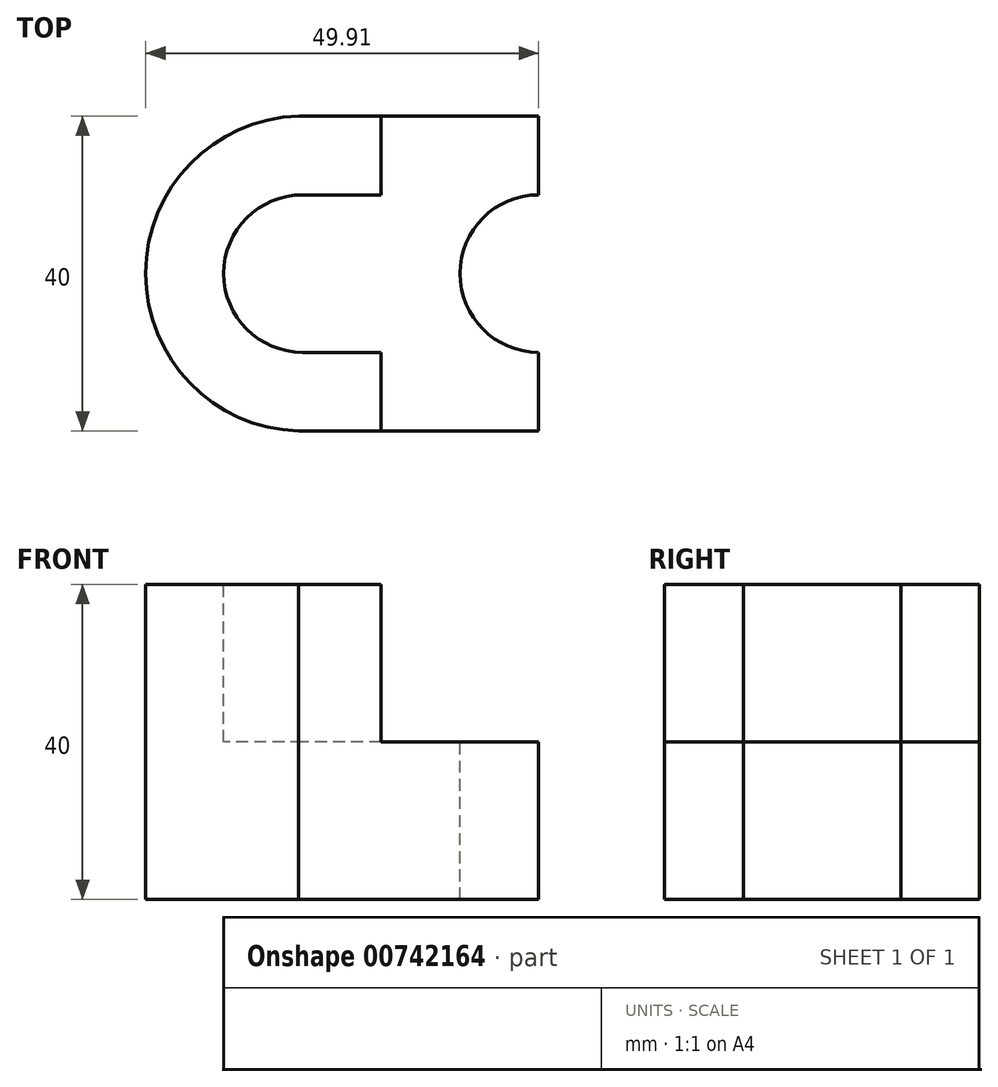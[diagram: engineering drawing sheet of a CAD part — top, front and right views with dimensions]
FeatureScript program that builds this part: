
annotation { "Feature Type Name" : "Feature", "Feature Type Description" : "" }
export const myFeature = defineFeature(function(context is Context, id is Id, definition is map)
    precondition{}
    {
        {
            var Q0;
            Q0=qCreatedBy(makeId("Front.planeOp"),FACE);
            var sketch = newSketch(context, id + "F0", { "sketchPlane" : qUnion([Q0])});
            skLineSegment(sketch, "E0", {"start": v(0, 0) * mm, "end": v(50, 0) * mm});
            skLineSegment(sketch, "E1", {"start": v(50, 0) * mm, "end": v(50, 20) * mm});
            skLineSegment(sketch, "E2", {"start": v(50, 20) * mm, "end": v(30, 20) * mm});
            skLineSegment(sketch, "E3", {"start": v(30, 20) * mm, "end": v(30, 40) * mm});
            skLineSegment(sketch, "E4", {"start": v(30, 40) * mm, "end": v(0, 40) * mm});
            skLineSegment(sketch, "E5", {"start": v(0, 40) * mm, "end": v(0, 0) * mm});
            skSolve(sketch);
        }
        {
            var Q0;
            Q0=makeQuery(id+"F0.imprint","IMPRINT",FACE,{"disambiguationData":[TD([[makeQuery(id+"F0.imprint","IMPRINT",EDGE,{"derivedFrom":sQuery(id+"F0.wireOp",EDGE,"E0")}),1.0]])]});
            extrude(context, id + "F1", {"entities" : qUnion([Q0]), "depth" : 40 * mm, "offsetDistance" : 25 * mm});
        }
        {
            var Q0;
            Q0=makeQuery(id+"F1.opExtrude","SWEPT_FACE",FACE,{"disambiguationData":[OSD([sQuery(id+"F0.wireOp",EDGE,"E4")])]});
            var sketch = newSketch(context, id + "F2", { "sketchPlane" : qUnion([Q0])});
            skArc(sketch, "E6", {"start": v(19.56, 0) * mm, "mid": v(0.1, -20.57) * mm, "end": v(20.7, -40) * mm});
            skSolve(sketch);
        }
        {
            var Q0;
            {var subQ1=sQuery(id+"F0.wireOp",EDGE,"E4");var subQ6=makeQuery(id+"F1.opExtrude","SWEPT_EDGE",EDGE,{"disambiguationData":[OSD([subQ1,sQuery(id+"F0.wireOp",EDGE,"E5")])]});Q0=makeQuery(id+"F2.imprint","IMPRINT",FACE,{"disambiguationData":[TD([[makeQuery(id+"F2.imprint","IMPRINT",EDGE,{"derivedFrom":subQ6}),-1.0]])]});}
            extrude(context, id + "F3", {"entities" : qUnion([Q0]), "operationType" : NewBodyOperationType.REMOVE, "oppositeDirection" : true, "depth" : 40 * mm, "offsetDistance" : 25 * mm});
        }
        {
            var Q0;
            Q0=makeQuery(id+"F1.opExtrude","SWEPT_FACE",FACE,{"disambiguationData":[OSD([sQuery(id+"F0.wireOp",EDGE,"E4")])]});
            var sketch = newSketch(context, id + "F4", { "sketchPlane" : qUnion([Q0])});
            skLineSegment(sketch, "E7", {"start": v(30, 0) * mm, "end": v(30, -10) * mm});
            skLineSegment(sketch, "E8", {"start": v(30, -10) * mm, "end": v(20, -10) * mm});
            skLineSegment(sketch, "E9", {"start": v(20, -10) * mm, "end": v(20, -30) * mm});
            skLineSegment(sketch, "E10", {"start": v(20, -30) * mm, "end": v(30, -30) * mm});
            skLineSegment(sketch, "E11", {"start": v(30, -30) * mm, "end": v(30, -40) * mm});
            skLineSegment(sketch, "E12", {"start": v(30, -10) * mm, "end": v(30, -30) * mm});
            skSolve(sketch);
        }
        {
            var Q0;
            Q0=makeQuery(id+"F4.imprint","IMPRINT",FACE,{"disambiguationData":[TD([[makeQuery(id+"F4.imprint","IMPRINT",EDGE,{"derivedFrom":sQuery(id+"F4.wireOp",EDGE,"E8")}),1.0]])]});
            extrude(context, id + "F5", {"entities" : qUnion([Q0]), "operationType" : NewBodyOperationType.REMOVE, "oppositeDirection" : true, "depth" : 20 * mm, "offsetDistance" : 25 * mm});
        }
        {
            var Q0;
            Q0=makeQuery(id+"F1.opExtrude","SWEPT_FACE",FACE,{"disambiguationData":[OSD([sQuery(id+"F0.wireOp",EDGE,"E4")])]});
            var sketch = newSketch(context, id + "F6", { "sketchPlane" : qUnion([Q0])});
            skArc(sketch, "E13", {"start": v(20, -10) * mm, "mid": v(10, -20) * mm, "end": v(20, -30) * mm});
            skSolve(sketch);
        }
        {
            var Q0;
            Q0=makeQuery(id+"F6.imprint","IMPRINT",FACE,{"disambiguationData":[TD([[makeQuery(id+"F6.imprint","IMPRINT",EDGE,{"derivedFrom":sQuery(id+"F6.wireOp",EDGE,"E13")}),1.0]])]});
            extrude(context, id + "F7", {"entities" : qUnion([Q0]), "operationType" : NewBodyOperationType.REMOVE, "oppositeDirection" : true, "depth" : 20 * mm, "offsetDistance" : 25 * mm});
        }
        {
            var Q0;
            {var subQ0=sQuery(id+"F4.wireOp",EDGE,"E9");Q0=makeQuery(id+"F7.boolean.opBoolean","MERGE",FACE,{"derivedFrom":[makeQuery(id+"F5.boolean.opBoolean","MERGE",FACE,{"derivedFrom":[makeQuery(id+"F1.opExtrude","SWEPT_FACE",FACE,{"disambiguationData":[OSD([sQuery(id+"F0.wireOp",EDGE,"E2")])]}),makeQuery(id+"F5.opExtrude","CAP_FACE",FACE,{"disambiguationData":[OSD([sQuery(id+"F4.wireOp",EDGE,"E8"),subQ0,sQuery(id+"F4.wireOp",EDGE,"E10"),sQuery(id+"F4.wireOp",EDGE,"E12")])],"isStart":false})]}),makeQuery(id+"F7.opExtrude","CAP_FACE",FACE,{"disambiguationData":[OSD([subQ0,sQuery(id+"F6.wireOp",EDGE,"E13")])],"isStart":false})]});}
            var sketch = newSketch(context, id + "F8", { "sketchPlane" : qUnion([Q0])});
            skCircle(sketch, "E14", {"center": v(50, -20) * mm, "radius": 10 * mm});
            skSolve(sketch);
        }
        {
            var Q0;
            {var subQ0=sQuery(id+"F8.wireOp",EDGE,"E14");var subQ1=makeQuery(id+"F1.opExtrude","SWEPT_EDGE",EDGE,{"disambiguationData":[OSD([sQuery(id+"F0.wireOp",EDGE,"E1"),sQuery(id+"F0.wireOp",EDGE,"E2")])]});var subQ2=makeQuery(id+"F8.imprint","INTERSECT",VERTEX,{"disambiguationData":[OD(0.0)],"derivedFrom":[subQ1,subQ0]});Q0=makeQuery(id+"F8.imprint","IMPRINT",FACE,{"disambiguationData":[TD([[makeQuery(id+"F8.imprint","IMPRINT",EDGE,{"disambiguationData":[TD([[subQ2,-1.0]])],"derivedFrom":subQ0}),1.0]])]});}
            extrude(context, id + "F9", {"entities" : qUnion([Q0]), "operationType" : NewBodyOperationType.REMOVE, "oppositeDirection" : true, "depth" : 20 * mm, "offsetDistance" : 25 * mm});
        }
    });
